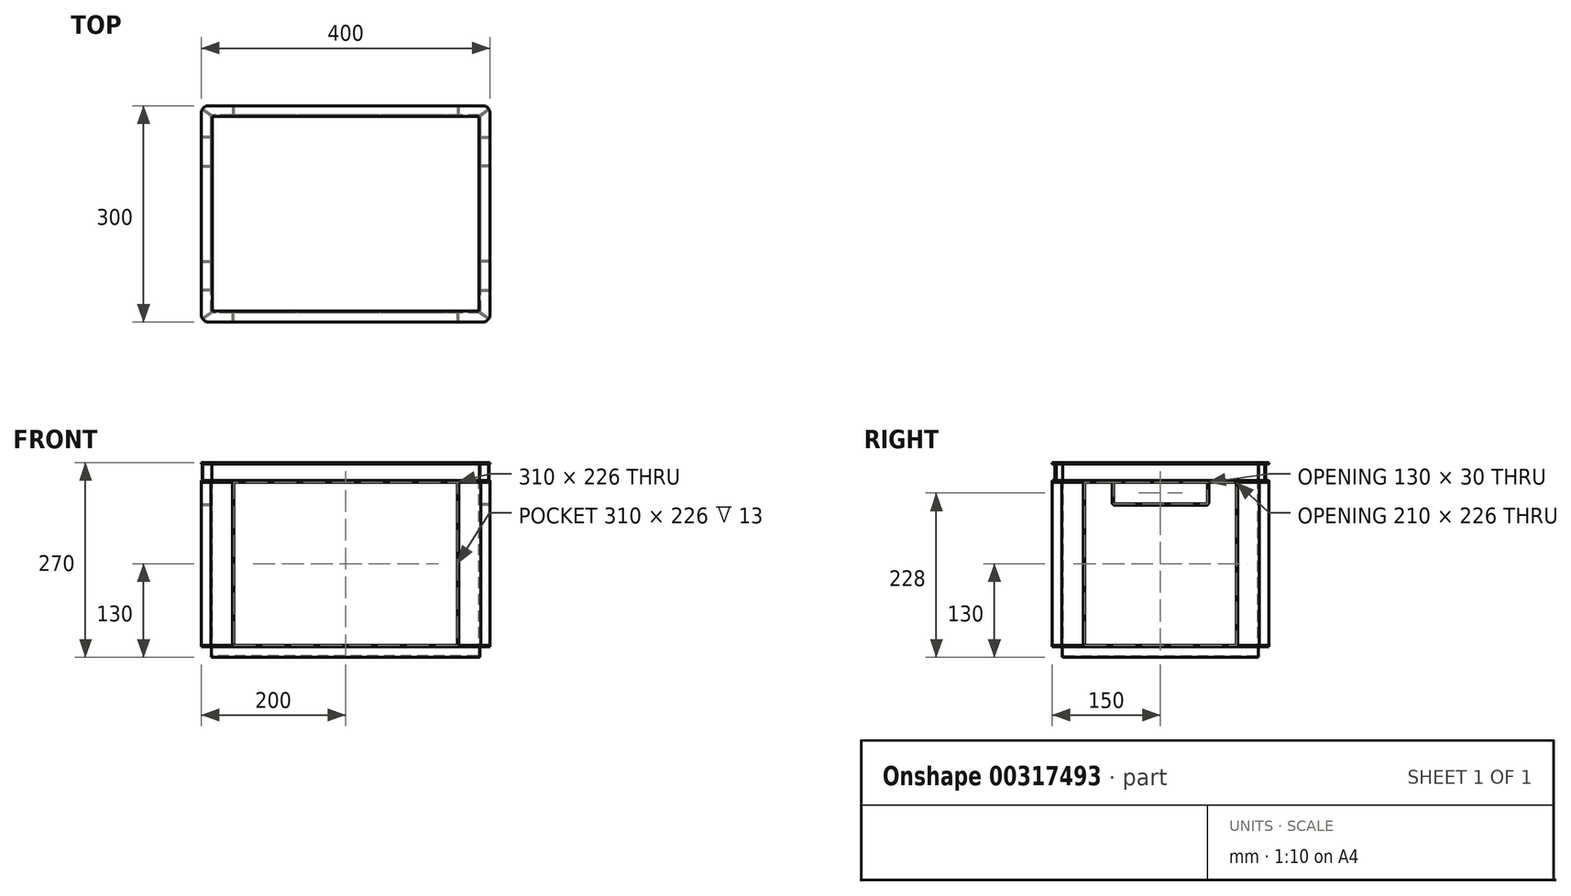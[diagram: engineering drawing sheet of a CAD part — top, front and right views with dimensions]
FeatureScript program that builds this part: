
annotation { "Feature Type Name" : "Feature", "Feature Type Description" : "" }
export const myFeature = defineFeature(function(context is Context, id is Id, definition is map)
    precondition{}
    {
        {
            var Q0;
            Q0=qCreatedBy(makeId("Top.planeOp"),FACE);
            var sketch = newSketch(context, id + "F0", { "sketchPlane" : qUnion([Q0])});
            skLineSegment(sketch, "E0.bottom", {"start": v(186, -136) * mm, "end": v(-186, -136) * mm});
            skLineSegment(sketch, "E0.top", {"start": v(186, 136) * mm, "end": v(-186, 136) * mm});
            skLineSegment(sketch, "E0.left", {"start": v(186, -136) * mm, "end": v(186, 136) * mm});
            skLineSegment(sketch, "E0.right", {"start": v(-186, -136) * mm, "end": v(-186, 136) * mm});
            skPoint(sketch, "E0.middle", {"position": v(0, 0) * mm});
            skPoint(sketch, "E1.visualSharp", {"position": v(-186, 136) * mm});
            skPoint(sketch, "E2.visualSharp", {"position": v(186, 136) * mm});
            skPoint(sketch, "E3.visualSharp", {"position": v(186, -136) * mm});
            skPoint(sketch, "E4.visualSharp", {"position": v(-186, -136) * mm});
            skSolve(sketch);
        }
        {
            var Q0;
            Q0=qSketchRegion(id+"F0",true);
            extrude(context, id + "F1", {"entities" : qUnion([Q0]), "depth" : 15 * mm});
        }
        {
            var Q0;
            Q0=makeQuery(id+"F1.opExtrude","CAP_FACE",FACE,{"disambiguationData":[OSD([sQuery(id+"F0.wireOp",EDGE,"E0.bottom"),sQuery(id+"F0.wireOp",EDGE,"E0.top"),sQuery(id+"F0.wireOp",EDGE,"E0.left"),sQuery(id+"F0.wireOp",EDGE,"E0.right")])],"isStart":false});
            var sketch = newSketch(context, id + "F2", { "sketchPlane" : qUnion([Q0])});
            skLineSegment(sketch, "E5.bottom", {"start": v(190, -150) * mm, "end": v(-190, -150) * mm});
            skLineSegment(sketch, "E5.top", {"start": v(190, 150) * mm, "end": v(-190, 150) * mm});
            skLineSegment(sketch, "E5.left", {"start": v(200, -140) * mm, "end": v(200, 140) * mm});
            skLineSegment(sketch, "E5.right", {"start": v(-200, -140) * mm, "end": v(-200, 140) * mm});
            skPoint(sketch, "E5.middle", {"position": v(0, 0) * mm});
            skPoint(sketch, "E6.visualSharp", {"position": v(-200, 150) * mm});
            skArc(sketch, "E6.filletArc", {"start": v(-190, 150) * mm, "mid": v(-197.07, 147.07) * mm, "end": v(-200, 140) * mm});
            skPoint(sketch, "E7.visualSharp", {"position": v(200, 150) * mm});
            skArc(sketch, "E7.filletArc", {"start": v(200, 140) * mm, "mid": v(197.07, 147.07) * mm, "end": v(190, 150) * mm});
            skPoint(sketch, "E8.visualSharp", {"position": v(200, -150) * mm});
            skArc(sketch, "E8.filletArc", {"start": v(190, -150) * mm, "mid": v(197.07, -147.07) * mm, "end": v(200, -140) * mm});
            skPoint(sketch, "E9.visualSharp", {"position": v(-200, -150) * mm});
            skArc(sketch, "E9.filletArc", {"start": v(-200, -140) * mm, "mid": v(-197.07, -147.07) * mm, "end": v(-190, -150) * mm});
            skSolve(sketch);
        }
        {
            var Q0;
            Q0=makeQuery(id+"F2.imprint","IMPRINT",FACE,{"disambiguationData":[TD([[makeQuery(id+"F2.imprint","IMPRINT",EDGE,{"derivedFrom":makeQuery(id+"F1.opExtrude","CAP_EDGE",EDGE,{"disambiguationData":[OSD([sQuery(id+"F0.wireOp",EDGE,"E0.bottom")])],"isStart":false})}),-1.0]])]});
            var Q1;
            Q1=makeQuery(id+"F2.imprint","IMPRINT",FACE,{"disambiguationData":[TD([[makeQuery(id+"F2.imprint","IMPRINT",EDGE,{"derivedFrom":sQuery(id+"F2.wireOp",EDGE,"E5.bottom")}),-1.0]])]});
            extrude(context, id + "F3", {"entities" : qUnion([Q0, Q1]), "operationType" : NewBodyOperationType.ADD, "depth" : 2 * mm});
        }
        {
            var Q0;
            Q0=makeQuery(id+"F3.opExtrude","CAP_FACE",FACE,{"disambiguationData":[OSD([sQuery(id+"F2.wireOp",EDGE,"E5.bottom"),sQuery(id+"F2.wireOp",EDGE,"E5.top"),sQuery(id+"F2.wireOp",EDGE,"E5.left"),sQuery(id+"F2.wireOp",EDGE,"E5.right"),sQuery(id+"F2.wireOp",EDGE,"E6.filletArc"),sQuery(id+"F2.wireOp",EDGE,"E7.filletArc"),sQuery(id+"F2.wireOp",EDGE,"E8.filletArc"),sQuery(id+"F2.wireOp",EDGE,"E9.filletArc")])],"isStart":false});
            var sketch = newSketch(context, id + "F4", { "sketchPlane" : qUnion([Q0])});
            skLineSegment(sketch, "E10.bottom", {"start": v(187, -137) * mm, "end": v(157, -137) * mm});
            skLineSegment(sketch, "E10.top", {"start": v(187, 137) * mm, "end": v(157, 137) * mm});
            skLineSegment(sketch, "E10.left", {"start": v(187, -137) * mm, "end": v(187, -107) * mm});
            skLineSegment(sketch, "E10.right", {"start": v(-187, -137) * mm, "end": v(-187, -107) * mm});
            skPoint(sketch, "E10.middle", {"position": v(0, 0) * mm});
            skLineSegment(sketch, "E11.bottom", {"start": v(-155, -150) * mm, "end": v(-157, -150) * mm});
            skLineSegment(sketch, "E11.left", {"start": v(-155, -150) * mm, "end": v(-155, -137) * mm});
            skLineSegment(sketch, "E11.right", {"start": v(-157, -150) * mm, "end": v(-157, -137) * mm});
            skPoint(sketch, "E11.middle", {"position": v(-156, -143.5) * mm});
            skLineSegment(sketch, "E12.trimOffspring", {"start": v(-157, -137) * mm, "end": v(-187, -137) * mm});
            skLineSegment(sketch, "E13.bottom", {"start": v(-187, -107) * mm, "end": v(-200, -107) * mm});
            skLineSegment(sketch, "E13.top", {"start": v(-187, -105) * mm, "end": v(-200, -105) * mm});
            skLineSegment(sketch, "E13.right", {"start": v(-200, -107) * mm, "end": v(-200, -105) * mm});
            skPoint(sketch, "E13.middle", {"position": v(-193.5, -106) * mm});
            skLineSegment(sketch, "E14.trimOffspring", {"start": v(-187, -105) * mm, "end": v(-187, 105) * mm});
            skLineSegment(sketch, "E15.MirrorCS", {"start": v(200, -107) * mm, "end": v(200, -105) * mm});
            skLineSegment(sketch, "E16.MirrorCS", {"start": v(155, -150) * mm, "end": v(155, -137) * mm});
            skLineSegment(sketch, "E17.MirrorCS", {"start": v(155, -150) * mm, "end": v(157, -150) * mm});
            skLineSegment(sketch, "E18.MirrorCS", {"start": v(157, -150) * mm, "end": v(157, -137) * mm});
            skLineSegment(sketch, "E19.MirrorCS", {"start": v(187, -105) * mm, "end": v(200, -105) * mm});
            skLineSegment(sketch, "E20.MirrorCS", {"start": v(187, -107) * mm, "end": v(200, -107) * mm});
            skPoint(sketch, "E21.MirrorP", {"position": v(193.5, -106) * mm});
            skLineSegment(sketch, "E22.trimOffspring", {"start": v(187, -105) * mm, "end": v(187, 105) * mm});
            skLineSegment(sketch, "E23.trimOffspring", {"start": v(155, -137) * mm, "end": v(-155, -137) * mm});
            skLineSegment(sketch, "E24.MirrorCS", {"start": v(-200, 107) * mm, "end": v(-200, 105) * mm});
            skPoint(sketch, "E25.MirrorP", {"position": v(-193.5, 106) * mm});
            skLineSegment(sketch, "E26.MirrorCS", {"start": v(-187, 105) * mm, "end": v(-200, 105) * mm});
            skLineSegment(sketch, "E27.MirrorCS", {"start": v(-187, 107) * mm, "end": v(-200, 107) * mm});
            skLineSegment(sketch, "E28.MirrorCS", {"start": v(-155, 150) * mm, "end": v(-157, 150) * mm});
            skLineSegment(sketch, "E29.MirrorCS", {"start": v(-157, 150) * mm, "end": v(-157, 137) * mm});
            skPoint(sketch, "E30.MirrorP", {"position": v(-156, 143.5) * mm});
            skLineSegment(sketch, "E31.MirrorCS", {"start": v(-155, 150) * mm, "end": v(-155, 137) * mm});
            skLineSegment(sketch, "E32.MirrorCS", {"start": v(155, 150) * mm, "end": v(157, 150) * mm});
            skLineSegment(sketch, "E33.MirrorCS", {"start": v(155, 150) * mm, "end": v(155, 137) * mm});
            skLineSegment(sketch, "E34.MirrorCS", {"start": v(157, 150) * mm, "end": v(157, 137) * mm});
            skLineSegment(sketch, "E35.MirrorCS", {"start": v(200, 107) * mm, "end": v(200, 105) * mm});
            skLineSegment(sketch, "E36.MirrorCS", {"start": v(187, 105) * mm, "end": v(200, 105) * mm});
            skPoint(sketch, "E37.MirrorP", {"position": v(193.5, 106) * mm});
            skLineSegment(sketch, "E38.MirrorCS", {"start": v(187, 107) * mm, "end": v(200, 107) * mm});
            skLineSegment(sketch, "E39.trimOffspring", {"start": v(-187, 107) * mm, "end": v(-187, 137) * mm});
            skLineSegment(sketch, "E40.trimOffspring", {"start": v(-157, 137) * mm, "end": v(-187, 137) * mm});
            skLineSegment(sketch, "E41.trimOffspring", {"start": v(155, 137) * mm, "end": v(-155, 137) * mm});
            skLineSegment(sketch, "E42.trimOffspring", {"start": v(187, 107) * mm, "end": v(187, 137) * mm});
            skSolve(sketch);
        }
        {
            var Q0;
            Q0=qSketchRegion(id+"F4",true);
            extrude(context, id + "F5", {"entities" : qUnion([Q0]), "operationType" : NewBodyOperationType.ADD, "depth" : (176 + 50) * mm});
        }
        {
            var Q0;
            Q0=makeQuery(id+"F5.opExtrude","CAP_FACE",FACE,{"disambiguationData":[OSD([sQuery(id+"F4.wireOp",EDGE,"E10.bottom"),sQuery(id+"F4.wireOp",EDGE,"E10.top"),sQuery(id+"F4.wireOp",EDGE,"E10.left"),sQuery(id+"F4.wireOp",EDGE,"E10.right")])],"isStart":false});
            var sketch = newSketch(context, id + "F6", { "sketchPlane" : qUnion([Q0])});
            skArc(sketch, "E43.0", {"start": v(-190, 150) * mm, "mid": v(-197.07, 147.07) * mm, "end": v(-200, 140) * mm});
            skArc(sketch, "E43.1", {"start": v(-200, -140) * mm, "mid": v(-197.07, -147.07) * mm, "end": v(-190, -150) * mm});
            skArc(sketch, "E43.2", {"start": v(190, -150) * mm, "mid": v(197.07, -147.07) * mm, "end": v(200, -140) * mm});
            skArc(sketch, "E43.3", {"start": v(200, 140) * mm, "mid": v(197.07, 147.07) * mm, "end": v(190, 150) * mm});
            skLineSegment(sketch, "E44", {"start": v(-200, 140) * mm, "end": v(-200, -140) * mm});
            skLineSegment(sketch, "E45", {"start": v(-190, -150) * mm, "end": v(190, -150) * mm});
            skLineSegment(sketch, "E46", {"start": v(200, 140) * mm, "end": v(200, -140) * mm});
            skLineSegment(sketch, "E47", {"start": v(-190, 150) * mm, "end": v(190, 150) * mm});
            skSolve(sketch);
        }
        {
            var Q0;
            Q0=qSketchRegion(id+"F6",true);
            extrude(context, id + "F7", {"entities" : qUnion([Q0]), "operationType" : NewBodyOperationType.ADD, "depth" : 2 * mm});
        }
        {
            var Q0;
            Q0=makeQuery(id+"F7.opExtrude","CAP_FACE",FACE,{"disambiguationData":[OSD([sQuery(id+"F6.wireOp",EDGE,"E43.0"),sQuery(id+"F6.wireOp",EDGE,"E43.1"),sQuery(id+"F6.wireOp",EDGE,"E43.2"),sQuery(id+"F6.wireOp",EDGE,"E43.3"),sQuery(id+"F6.wireOp",EDGE,"E44"),sQuery(id+"F6.wireOp",EDGE,"E45"),sQuery(id+"F6.wireOp",EDGE,"E46"),sQuery(id+"F6.wireOp",EDGE,"E47")])],"isStart":false});
            var sketch = newSketch(context, id + "F8", { "sketchPlane" : qUnion([Q0])});
            skLineSegment(sketch, "E48.bottom", {"start": v(185.3, -137) * mm, "end": v(-185.3, -137) * mm});
            skLineSegment(sketch, "E48.top", {"start": v(185.3, 137) * mm, "end": v(-185.3, 137) * mm});
            skLineSegment(sketch, "E48.left", {"start": v(187, -135.76) * mm, "end": v(187, 135.76) * mm});
            skLineSegment(sketch, "E48.right", {"start": v(-187, -135.76) * mm, "end": v(-187, 135.76) * mm});
            skPoint(sketch, "E48.middle", {"position": v(0, 0) * mm});
            skLineSegment(sketch, "E49", {"start": v(-187, 137) * mm, "end": v(187, -137) * mm, "construction": true});
            skLineSegment(sketch, "E50.0", {"start": v(-198.93, 144.5) * mm, "end": v(-187, 135.76) * mm});
            skLineSegment(sketch, "E51.0", {"start": v(-197.85, 146.2) * mm, "end": v(-185.3, 137) * mm});
            skArc(sketch, "E52.0", {"start": v(-197.85, 146.2) * mm, "mid": v(-198.43, 145.37) * mm, "end": v(-198.93, 144.5) * mm});
            skPoint(sketch, "E53.orphan", {"position": v(-190, 150) * mm});
            skPoint(sketch, "E54.orphan", {"position": v(-200, 140) * mm});
            skArc(sketch, "E55.0", {"start": v(197.85, -146.2) * mm, "mid": v(198.43, -145.37) * mm, "end": v(198.93, -144.5) * mm});
            skPoint(sketch, "E56.orphan", {"position": v(200, -140) * mm});
            skPoint(sketch, "E57.orphan", {"position": v(190, -150) * mm});
            skLineSegment(sketch, "E58.trimOffspring", {"start": v(187, -135.76) * mm, "end": v(198.93, -144.5) * mm});
            skLineSegment(sketch, "E59.trimOffspring", {"start": v(185.3, -137) * mm, "end": v(197.85, -146.2) * mm});
            skLineSegment(sketch, "E60.MirrorCS", {"start": v(-197.85, -146.2) * mm, "end": v(-185.3, -137) * mm});
            skPoint(sketch, "E61.MirrorP", {"position": v(-200, -140) * mm});
            skArc(sketch, "E62.MirrorCS", {"start": v(-197.85, -146.2) * mm, "mid": v(-198.43, -145.37) * mm, "end": v(-198.93, -144.5) * mm});
            skLineSegment(sketch, "E63.MirrorCS", {"start": v(-198.93, -144.5) * mm, "end": v(-187, -135.76) * mm});
            skPoint(sketch, "E64.MirrorP", {"position": v(-190, -150) * mm});
            skArc(sketch, "E65.MirrorCS", {"start": v(197.85, 146.2) * mm, "mid": v(198.43, 145.37) * mm, "end": v(198.93, 144.5) * mm});
            skPoint(sketch, "E66.MirrorP", {"position": v(200, 140) * mm});
            skPoint(sketch, "E67.MirrorP", {"position": v(190, 150) * mm});
            skLineSegment(sketch, "E68.MirrorCS", {"start": v(187, 135.76) * mm, "end": v(198.93, 144.5) * mm});
            skLineSegment(sketch, "E69.MirrorCS", {"start": v(185.3, 137) * mm, "end": v(197.85, 146.2) * mm});
            skPoint(sketch, "E70.orphan", {"position": v(187, 137) * mm});
            skPoint(sketch, "E71.orphan", {"position": v(-187, -137) * mm});
            skSolve(sketch);
        }
        {
            var Q0;
            Q0=qSketchRegion(id+"F8",true);
            extrude(context, id + "F9", {"entities" : qUnion([Q0]), "operationType" : NewBodyOperationType.ADD, "depth" : 23 * mm});
        }
        {
            var Q0;
            Q0=makeQuery(id+"F9.opExtrude","CAP_FACE",FACE,{"disambiguationData":[OSD([sQuery(id+"F8.wireOp",EDGE,"E48.bottom"),sQuery(id+"F8.wireOp",EDGE,"E48.top"),sQuery(id+"F8.wireOp",EDGE,"E48.left"),sQuery(id+"F8.wireOp",EDGE,"E48.right"),sQuery(id+"F8.wireOp",EDGE,"E50.0"),sQuery(id+"F8.wireOp",EDGE,"E51.0"),sQuery(id+"F8.wireOp",EDGE,"E52.0"),sQuery(id+"F8.wireOp",EDGE,"E55.0"),sQuery(id+"F8.wireOp",EDGE,"E58.trimOffspring"),sQuery(id+"F8.wireOp",EDGE,"E59.trimOffspring"),sQuery(id+"F8.wireOp",EDGE,"E60.MirrorCS"),sQuery(id+"F8.wireOp",EDGE,"E62.MirrorCS"),sQuery(id+"F8.wireOp",EDGE,"E63.MirrorCS"),sQuery(id+"F8.wireOp",EDGE,"E65.MirrorCS"),sQuery(id+"F8.wireOp",EDGE,"E68.MirrorCS"),sQuery(id+"F8.wireOp",EDGE,"E69.MirrorCS")])],"isStart":false});
            var sketch = newSketch(context, id + "F10", { "sketchPlane" : qUnion([Q0])});
            skArc(sketch, "E72.0", {"start": v(190, -150) * mm, "mid": v(197.07, -147.07) * mm, "end": v(200, -140) * mm});
            skArc(sketch, "E73.0", {"start": v(-200, -140) * mm, "mid": v(-197.07, -147.07) * mm, "end": v(-190, -150) * mm});
            skArc(sketch, "E74.0", {"start": v(200, 140) * mm, "mid": v(197.07, 147.07) * mm, "end": v(190, 150) * mm});
            skLineSegment(sketch, "E75.0", {"start": v(200, -140) * mm, "end": v(200, 140) * mm});
            skLineSegment(sketch, "E76.0", {"start": v(190, 150) * mm, "end": v(-190, 150) * mm});
            skLineSegment(sketch, "E77.0", {"start": v(190, -150) * mm, "end": v(-190, -150) * mm});
            skLineSegment(sketch, "E78.0", {"start": v(-200, -140) * mm, "end": v(-200, 140) * mm});
            skArc(sketch, "E79.0", {"start": v(-190, 150) * mm, "mid": v(-197.07, 147.07) * mm, "end": v(-200, 140) * mm});
            skSolve(sketch);
        }
        {
            var Q0;
            Q0=qSketchRegion(id+"F10",true);
            extrude(context, id + "F11", {"entities" : qUnion([Q0]), "operationType" : NewBodyOperationType.ADD, "depth" : 2 * mm});
        }
        {
            var Q0;
            Q0=makeQuery(id+"F11.opExtrude","CAP_FACE",FACE,{"disambiguationData":[OSD([sQuery(id+"F10.wireOp",EDGE,"E72.0"),sQuery(id+"F10.wireOp",EDGE,"E73.0"),sQuery(id+"F10.wireOp",EDGE,"E74.0"),sQuery(id+"F10.wireOp",EDGE,"E75.0"),sQuery(id+"F10.wireOp",EDGE,"E76.0"),sQuery(id+"F10.wireOp",EDGE,"E77.0"),sQuery(id+"F10.wireOp",EDGE,"E78.0"),sQuery(id+"F10.wireOp",EDGE,"E79.0")])],"isStart":false});
            var sketch = newSketch(context, id + "F12", { "sketchPlane" : qUnion([Q0])});
            skLineSegment(sketch, "E80.bottom", {"start": v(185, -135) * mm, "end": v(-185, -135) * mm});
            skLineSegment(sketch, "E80.top", {"start": v(185, 135) * mm, "end": v(-185, 135) * mm});
            skLineSegment(sketch, "E80.left", {"start": v(185, -135) * mm, "end": v(185, 135) * mm});
            skLineSegment(sketch, "E80.right", {"start": v(-185, -135) * mm, "end": v(-185, 135) * mm});
            skPoint(sketch, "E80.middle", {"position": v(0, 0) * mm});
            skSolve(sketch);
        }
        {
            var Q0;
            Q0=qSketchRegion(id+"F12",true);
            extrude(context, id + "F13", {"entities" : qUnion([Q0]), "operationType" : NewBodyOperationType.REMOVE, "oppositeDirection" : true, "depth" : (218 + 50) * mm});
        }
        {
            var Q0;
            Q0=makeQuery(id+"F5.opExtrude","SWEPT_FACE",FACE,{"disambiguationData":[OSD([sQuery(id+"F4.wireOp",EDGE,"E14.trimOffspring")])]});
            var sketch = newSketch(context, id + "F14", { "sketchPlane" : qUnion([Q0])});
            skLineSegment(sketch, "E81.bottom", {"start": v(63, 211) * mm, "end": v(-63, 211) * mm});
            skLineSegment(sketch, "E81.left", {"start": v(67, 215) * mm, "end": v(67, 243) * mm});
            skLineSegment(sketch, "E81.right", {"start": v(-67, 215) * mm, "end": v(-67, 243) * mm});
            skPoint(sketch, "E81.middle", {"position": v(0, 148.17) * mm});
            skLineSegment(sketch, "E82.bottom", {"start": v(63, 213) * mm, "end": v(-63, 213) * mm});
            skLineSegment(sketch, "E82.left", {"start": v(65, 215) * mm, "end": v(65, 243) * mm});
            skLineSegment(sketch, "E82.right", {"start": v(-65, 215) * mm, "end": v(-65, 243) * mm});
            skLineSegment(sketch, "E83.0", {"start": v(-67, 243) * mm, "end": v(-65, 243) * mm});
            skPoint(sketch, "E84.orphan", {"position": v(-67, 85.34) * mm});
            skPoint(sketch, "E85.orphan", {"position": v(-65, 83.34) * mm});
            skPoint(sketch, "E86.orphan", {"position": v(65, 83.34) * mm});
            skPoint(sketch, "E87.orphan", {"position": v(67, 85.34) * mm});
            skLineSegment(sketch, "E88.trimOffspring", {"start": v(65, 243) * mm, "end": v(67, 243) * mm});
            skPoint(sketch, "E89.orphan", {"position": v(-105, 243) * mm});
            skPoint(sketch, "E90.orphan", {"position": v(105, 243) * mm});
            skPoint(sketch, "E91.visualSharp", {"position": v(-67, 211) * mm});
            skArc(sketch, "E91.filletArc", {"start": v(-67, 215) * mm, "mid": v(-65.83, 212.17) * mm, "end": v(-63, 211) * mm});
            skPoint(sketch, "E92.visualSharp", {"position": v(67, 211) * mm});
            skArc(sketch, "E92.filletArc", {"start": v(63, 211) * mm, "mid": v(65.83, 212.17) * mm, "end": v(67, 215) * mm});
            skPoint(sketch, "E93.visualSharp", {"position": v(65, 213) * mm});
            skArc(sketch, "E93.filletArc", {"start": v(63, 213) * mm, "mid": v(64.41, 213.59) * mm, "end": v(65, 215) * mm});
            skPoint(sketch, "E94.visualSharp", {"position": v(-65, 213) * mm});
            skArc(sketch, "E94.filletArc", {"start": v(-65, 215) * mm, "mid": v(-64.41, 213.59) * mm, "end": v(-63, 213) * mm});
            skSolve(sketch);
        }
        {
            var Q0;
            Q0=qSketchRegion(id+"F14",true);
            var Q1;
            Q1=makeQuery(id+"F7.boolean.opBoolean","MERGE",FACE,{"derivedFrom":[makeQuery(id+"F5.boolean.opBoolean","MERGE",FACE,{"derivedFrom":[makeQuery(id+"F3.opExtrude","SWEPT_FACE",FACE,{"disambiguationData":[OSD([sQuery(id+"F2.wireOp",EDGE,"E5.right")])]}),makeQuery(id+"F5.opExtrude","SWEPT_FACE",FACE,{"disambiguationData":[OSD([sQuery(id+"F4.wireOp",EDGE,"E13.right")])]}),makeQuery(id+"F5.opExtrude","SWEPT_FACE",FACE,{"disambiguationData":[OSD([sQuery(id+"F4.wireOp",EDGE,"E24.MirrorCS")])]})]}),makeQuery(id+"F7.opExtrude","SWEPT_FACE",FACE,{"disambiguationData":[OSD([sQuery(id+"F6.wireOp",EDGE,"E44")])]})]});
            extrude(context, id + "F15", {"entities" : qUnion([Q0]), "operationType" : NewBodyOperationType.ADD, "endBound" : BoundingType.UP_TO_SURFACE, "endBoundEntityFace" : qUnion([Q1]), "depth" : 25 * mm});
        }
        {
            var Q0;
            Q0=makeQuery(id+"F5.opExtrude","SWEPT_FACE",FACE,{"disambiguationData":[OSD([sQuery(id+"F4.wireOp",EDGE,"E22.trimOffspring")])]});
            var sketch = newSketch(context, id + "F16", { "sketchPlane" : qUnion([Q0])});
            skLineSegment(sketch, "E95.0", {"start": v(67, 215) * mm, "end": v(67, 243) * mm});
            skArc(sketch, "E95.1", {"start": v(67, 215) * mm, "mid": v(65.83, 212.17) * mm, "end": v(63, 211) * mm});
            skLineSegment(sketch, "E95.2", {"start": v(-63, 211) * mm, "end": v(63, 211) * mm});
            skLineSegment(sketch, "E95.3", {"start": v(-63, 213) * mm, "end": v(63, 213) * mm});
            skLineSegment(sketch, "E95.4", {"start": v(65, 215) * mm, "end": v(65, 243) * mm});
            skArc(sketch, "E95.5", {"start": v(65, 215) * mm, "mid": v(64.41, 213.59) * mm, "end": v(63, 213) * mm});
            skArc(sketch, "E95.6", {"start": v(-63, 213) * mm, "mid": v(-64.41, 213.59) * mm, "end": v(-65, 215) * mm});
            skArc(sketch, "E95.7", {"start": v(-63, 211) * mm, "mid": v(-65.83, 212.17) * mm, "end": v(-67, 215) * mm});
            skLineSegment(sketch, "E95.8", {"start": v(-67, 215) * mm, "end": v(-67, 243) * mm});
            skLineSegment(sketch, "E95.9", {"start": v(-65, 215) * mm, "end": v(-65, 243) * mm});
            skLineSegment(sketch, "E96", {"start": v(67, 243) * mm, "end": v(65, 243) * mm});
            skLineSegment(sketch, "E97", {"start": v(-65, 243) * mm, "end": v(-67, 243) * mm});
            skSolve(sketch);
        }
        {
            var Q0;
            Q0=qSketchRegion(id+"F16",true);
            var Q1;
            Q1=makeQuery(id+"F7.boolean.opBoolean","MERGE",FACE,{"derivedFrom":[makeQuery(id+"F5.boolean.opBoolean","MERGE",FACE,{"derivedFrom":[makeQuery(id+"F3.opExtrude","SWEPT_FACE",FACE,{"disambiguationData":[OSD([sQuery(id+"F2.wireOp",EDGE,"E5.left")])]}),makeQuery(id+"F5.opExtrude","SWEPT_FACE",FACE,{"disambiguationData":[OSD([sQuery(id+"F4.wireOp",EDGE,"E15.MirrorCS")])]}),makeQuery(id+"F5.opExtrude","SWEPT_FACE",FACE,{"disambiguationData":[OSD([sQuery(id+"F4.wireOp",EDGE,"E35.MirrorCS")])]})]}),makeQuery(id+"F7.opExtrude","SWEPT_FACE",FACE,{"disambiguationData":[OSD([sQuery(id+"F6.wireOp",EDGE,"E46")])]})]});
            extrude(context, id + "F17", {"entities" : qUnion([Q0]), "operationType" : NewBodyOperationType.ADD, "endBound" : BoundingType.UP_TO_SURFACE, "endBoundEntityFace" : qUnion([Q1]), "depth" : 25 * mm});
        }
        {
            var Q0;
            Q0=makeQuery(id+"F13.boolean.opBoolean","COPY",EDGE,{"derivedFrom":makeQuery(id+"F13.opExtrude","SWEPT_EDGE",EDGE,{"disambiguationData":[OSD([sQuery(id+"F12.wireOp",EDGE,"E80.bottom"),sQuery(id+"F12.wireOp",EDGE,"E80.right")])]})});
            var Q1;
            Q1=makeQuery(id+"F13.boolean.opBoolean","COPY",EDGE,{"derivedFrom":makeQuery(id+"F13.opExtrude","SWEPT_EDGE",EDGE,{"disambiguationData":[OSD([sQuery(id+"F12.wireOp",EDGE,"E80.bottom"),sQuery(id+"F12.wireOp",EDGE,"E80.left")])]})});
            var Q2;
            Q2=makeQuery(id+"F13.boolean.opBoolean","COPY",EDGE,{"derivedFrom":makeQuery(id+"F13.opExtrude","SWEPT_EDGE",EDGE,{"disambiguationData":[OSD([sQuery(id+"F12.wireOp",EDGE,"E80.top"),sQuery(id+"F12.wireOp",EDGE,"E80.left")])]})});
            var Q3;
            Q3=makeQuery(id+"F13.boolean.opBoolean","COPY",EDGE,{"derivedFrom":makeQuery(id+"F13.opExtrude","CAP_EDGE",EDGE,{"disambiguationData":[OSD([sQuery(id+"F12.wireOp",EDGE,"E80.top")])],"isStart":false})});
            var Q4;
            Q4=makeQuery(id+"F13.boolean.opBoolean","COPY",EDGE,{"derivedFrom":makeQuery(id+"F13.opExtrude","CAP_EDGE",EDGE,{"disambiguationData":[OSD([sQuery(id+"F12.wireOp",EDGE,"E80.left")])],"isStart":false})});
            var Q5;
            Q5=makeQuery(id+"F13.boolean.opBoolean","COPY",EDGE,{"derivedFrom":makeQuery(id+"F13.opExtrude","CAP_EDGE",EDGE,{"disambiguationData":[OSD([sQuery(id+"F12.wireOp",EDGE,"E80.bottom")])],"isStart":false})});
            var Q6;
            Q6=makeQuery(id+"F13.boolean.opBoolean","COPY",EDGE,{"derivedFrom":makeQuery(id+"F13.opExtrude","CAP_EDGE",EDGE,{"disambiguationData":[OSD([sQuery(id+"F12.wireOp",EDGE,"E80.right")])],"isStart":false})});
            var Q7;
            Q7=makeQuery(id+"F13.boolean.opBoolean","COPY",EDGE,{"derivedFrom":makeQuery(id+"F13.opExtrude","SWEPT_EDGE",EDGE,{"disambiguationData":[OSD([sQuery(id+"F12.wireOp",EDGE,"E80.top"),sQuery(id+"F12.wireOp",EDGE,"E80.right")])]})});
            var Q8;
            Q8=makeQuery(id+"F5.opExtrude","SWEPT_EDGE",EDGE,{"disambiguationData":[OSD([sQuery(id+"F4.wireOp",EDGE,"E10.bottom"),sQuery(id+"F4.wireOp",EDGE,"E10.left")])]});
            var Q9;
            Q9=makeQuery(id+"F5.opExtrude","SWEPT_EDGE",EDGE,{"disambiguationData":[OSD([sQuery(id+"F4.wireOp",EDGE,"E10.top"),sQuery(id+"F4.wireOp",EDGE,"E42.trimOffspring")])]});
            var Q10;
            Q10=makeQuery(id+"F5.opExtrude","SWEPT_EDGE",EDGE,{"disambiguationData":[OSD([sQuery(id+"F4.wireOp",EDGE,"E39.trimOffspring"),sQuery(id+"F4.wireOp",EDGE,"E40.trimOffspring")])]});
            var Q11;
            Q11=makeQuery(id+"F5.opExtrude","SWEPT_EDGE",EDGE,{"disambiguationData":[OSD([sQuery(id+"F4.wireOp",EDGE,"E10.right"),sQuery(id+"F4.wireOp",EDGE,"E12.trimOffspring")])]});
            var Q12;
            Q12=makeQuery(id+"F1.opExtrude","CAP_EDGE",EDGE,{"disambiguationData":[OSD([sQuery(id+"F0.wireOp",EDGE,"E0.left")])],"isStart":true});
            var Q13;
            Q13=makeQuery(id+"F1.opExtrude","CAP_EDGE",EDGE,{"disambiguationData":[OSD([sQuery(id+"F0.wireOp",EDGE,"E0.top")])],"isStart":true});
            var Q14;
            Q14=makeQuery(id+"F1.opExtrude","SWEPT_EDGE",EDGE,{"disambiguationData":[OSD([sQuery(id+"F0.wireOp",EDGE,"E0.top"),sQuery(id+"F0.wireOp",EDGE,"E0.left")])]});
            var Q15;
            Q15=makeQuery(id+"F1.opExtrude","CAP_EDGE",EDGE,{"disambiguationData":[OSD([sQuery(id+"F0.wireOp",EDGE,"E0.bottom")])],"isStart":true});
            var Q16;
            Q16=makeQuery(id+"F1.opExtrude","SWEPT_EDGE",EDGE,{"disambiguationData":[OSD([sQuery(id+"F0.wireOp",EDGE,"E0.bottom"),sQuery(id+"F0.wireOp",EDGE,"E0.left")])]});
            var Q17;
            Q17=makeQuery(id+"F1.opExtrude","SWEPT_EDGE",EDGE,{"disambiguationData":[OSD([sQuery(id+"F0.wireOp",EDGE,"E0.bottom"),sQuery(id+"F0.wireOp",EDGE,"E0.right")])]});
            var Q18;
            Q18=makeQuery(id+"F1.opExtrude","CAP_EDGE",EDGE,{"disambiguationData":[OSD([sQuery(id+"F0.wireOp",EDGE,"E0.right")])],"isStart":true});
            var Q19;
            Q19=makeQuery(id+"F1.opExtrude","SWEPT_EDGE",EDGE,{"disambiguationData":[OSD([sQuery(id+"F0.wireOp",EDGE,"E0.top"),sQuery(id+"F0.wireOp",EDGE,"E0.right")])]});
            fillet(context, id + "F18", {"entities" : qUnion([Q0, Q1, Q2, Q3, Q4, Q5, Q6, Q7, Q8, Q9, Q10, Q11, Q12, Q13, Q14, Q15, Q16, Q17, Q18, Q19]), "radius" : 2 * mm, "tangentPropagation" : true, "allowEdgeOverflow" : false});
        }
    });
